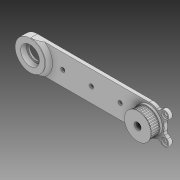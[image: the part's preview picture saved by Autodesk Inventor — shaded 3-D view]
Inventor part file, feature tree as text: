
AUTODESK INVENTOR PART (.ipt)
format: ipt  version: 2020 (Build 240168000, 168)  size: 423,936 bytes
history: native  units: mm
features: extrude x9, sketch x9, chamfer x2, plane x1, revolve x1, fillet x1, projected_geometry x1
ambient origin geometry x8: Origin, YZ Plane, XZ Plane, XY Plane, X Axis, Y Axis, Z Axis, Center Point
bodies: Solid1 (feature_tree)
feature tree (24):
  extrude  "Extrusion1"  Depth=13.0mm
  extrude  "Extrusion2"  Depth=6.0mm
  extrude  "Extrusion5"  Depth=10.0mm TaperAngle=0.0deg
  extrude  "Extrusion6"  Depth=25.0mm
  extrude  "Extrusion7"  Depth=25.0mm
  chamfer  "Chamfer2"  Distance=3.5mm
  plane  "Work Plane1"
  extrude  "Extrusion8"  Depth=1.5mm
  chamfer  "Chamfer3"  Distance=0.2mm
  revolve  "Revolution1"  [1 undecoded]
  extrude  "Extrusion10"  Depth=2.0mm
  fillet  "Fillet1"  Radius=1.74133mm
  extrude  "Extrusion11"  Depth=9.0mm
  extrude  "Extrusion14"  Depth=9.0mm TaperAngle=360.0deg
  sketch  "Sketch1"  dims[d0=13.0mm d1=100.3mm]
  sketch  "Sketch2"  dims[d2=3.0mm d3=0.0mm d4=6.0mm]
  sketch  "Sketch5"  dims[d6=16.3mm d7=10.0mm d8=0.0mm]
  sketch  "Sketch6"  dims[d18=3.5mm d19=25.0mm]
  sketch  "Sketch7"  dims[d20=25.0mm d21=16.3mm d22=3.5mm d23=0.0mm]
  projected_geometry  "Projected Loop1"
  sketch  "Sketch8"  dims[d24=5.0mm d25=0.0mm d26=1.5mm d27=0.2mm d28=0.0mm]
  sketch  "Sketch12"  dims[d29=3.0mm d30=2.0mm d31=45.0deg d32=23.0mm]
  sketch  "Sketch13"  dims[d33=-1.0mm d34=2.0mm d35=1.74133mm]
  sketch  "Sketch16"  dims[d36=1.2mm d37=0.65mm d38=360.0mm d40=360.0deg d42=7.0mm d43=0.0mm d44=0.6mm d45=2.0mm d46=45.0deg d60=90.0deg d61=3.2mm d62=7.5mm d64=10.0mm d65=10.0mm d66=0.0mm d67=2.0mm d68=6.0mm d69=1.5mm d70=0.0mm d91=8.1mm d92=9.0mm d93=0.0mm d71=0.872665mm]
note: 1 required parameter value undecoded (feature->parameter linkage not recoverable at this tier; creation-order binding heuristic only, values carry confidence <= 0.55)
